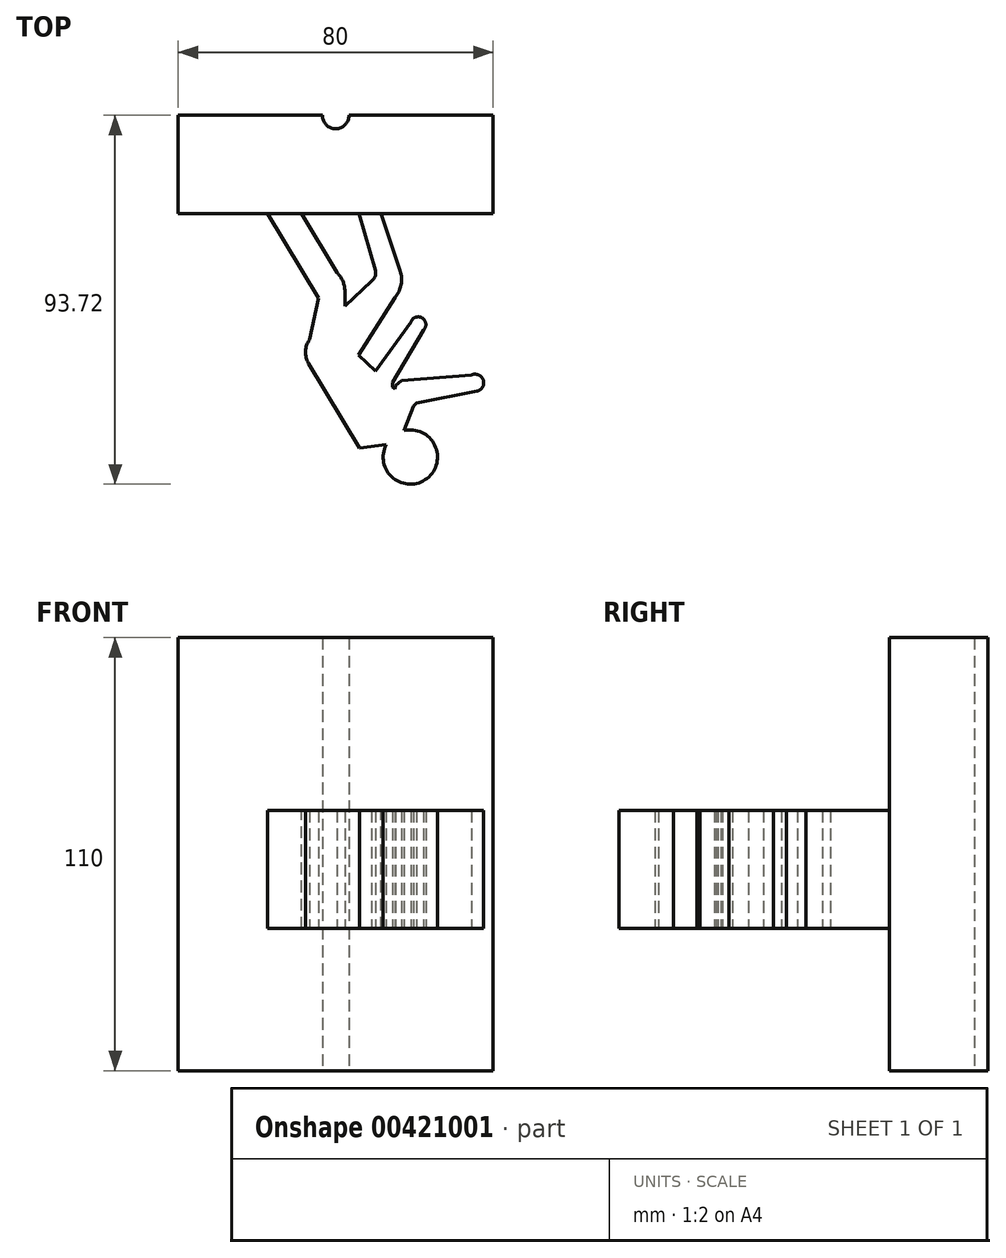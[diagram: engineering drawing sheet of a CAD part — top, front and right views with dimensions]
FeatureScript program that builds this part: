
annotation { "Feature Type Name" : "Feature", "Feature Type Description" : "" }
export const myFeature = defineFeature(function(context is Context, id is Id, definition is map)
    precondition{}
    {
        {
            var Q0;
            Q0=qCreatedBy(makeId("Front.planeOp"),FACE);
            var sketch = newSketch(context, id + "F0", { "sketchPlane" : qUnion([Q0])});
            skLineSegment(sketch, "E0.bottom", {"start": v(31.86, -51.09) * mm, "end": v(-48.14, -51.09) * mm});
            skLineSegment(sketch, "E0.top", {"start": v(31.86, 58.91) * mm, "end": v(-48.14, 58.91) * mm});
            skLineSegment(sketch, "E0.left", {"start": v(31.86, -51.09) * mm, "end": v(31.86, 58.91) * mm});
            skLineSegment(sketch, "E0.right", {"start": v(-48.14, -51.09) * mm, "end": v(-48.14, 58.91) * mm});
            skPoint(sketch, "E0.middle", {"position": v(-8.14, 3.91) * mm});
            skSolve(sketch);
        }
        {
            var Q0;
            Q0 = qSketchRegion(id + "F0", true);
            extrude(context, id + "F1", {"entities" : qUnion([Q0]), "depth" : 25 * mm});
        }
        {
            var Q0;
            Q0=makeQuery(id+"F1.opExtrude","SWEPT_FACE",FACE,{"disambiguationData":[OSD([sQuery(id+"F0.wireOp",EDGE,"E0.bottom")])]});
            var sketch = newSketch(context, id + "F2", { "sketchPlane" : qUnion([Q0])});
            skCircle(sketch, "E1", {"center": v(-8.14, 0) * mm, "radius": 3.4 * mm});
            skSolve(sketch);
        }
        {
            var Q0;
            {var subQ0=sQuery(id+"F2.wireOp",EDGE,"E1");var subQ1=makeQuery(id+"F1.opExtrude","CAP_EDGE",EDGE,{"disambiguationData":[OSD([sQuery(id+"F0.wireOp",EDGE,"E0.bottom")])],"isStart":true});var subQ2=makeQuery(id+"F2.imprint","INTERSECT",VERTEX,{"disambiguationData":[OD(0.0)],"derivedFrom":[subQ1,subQ0]});Q0=makeQuery(id+"F2.imprint","IMPRINT",FACE,{"disambiguationData":[TD([[makeQuery(id+"F2.imprint","IMPRINT",EDGE,{"disambiguationData":[TD([[subQ2,1.0]])],"derivedFrom":subQ0}),1.0]])]});}
            var Q1;
            {var subQ0=sQuery(id+"F2.wireOp",EDGE,"E1");var subQ1=makeQuery(id+"F1.opExtrude","CAP_EDGE",EDGE,{"disambiguationData":[OSD([sQuery(id+"F0.wireOp",EDGE,"E0.bottom")])],"isStart":true});var subQ2=makeQuery(id+"F2.imprint","INTERSECT",VERTEX,{"disambiguationData":[OD(0.0)],"derivedFrom":[subQ1,subQ0]});Q1=makeQuery(id+"F2.imprint","IMPRINT",FACE,{"disambiguationData":[TD([[makeQuery(id+"F2.imprint","IMPRINT",EDGE,{"disambiguationData":[TD([[subQ2,-1.0]])],"derivedFrom":subQ0}),1.0]])]});}
            extrude(context, id + "F3", {"entities" : qUnion([Q0, Q1]), "operationType" : NewBodyOperationType.REMOVE, "oppositeDirection" : true, "depth" : 122.9 * mm});
        }
        {
            var Q0;
            Q0=qCreatedBy(makeId("Top.planeOp"),FACE);
            var sketch = newSketch(context, id + "F4", { "sketchPlane" : qUnion([Q0])});
            skLineSegment(sketch, "E2", {"start": v(-12.54, -46.37) * mm, "end": v(-25.62, -24.68) * mm});
            skLineSegment(sketch, "E3", {"start": v(-17.04, -24.68) * mm, "end": v(-7.8, -40) * mm});
            skLineSegment(sketch, "E4", {"start": v(-14.79, -56.99) * mm, "end": v(-12.54, -46.37) * mm});
            skLineSegment(sketch, "E5", {"start": v(-5.8, -48.45) * mm, "end": v(0.9, -42.08) * mm});
            skLineSegment(sketch, "E6", {"start": v(1.95, -39.46) * mm, "end": v(-2.34, -24.68) * mm});
            skLineSegment(sketch, "E7", {"start": v(-2.34, -24.68) * mm, "end": v(3.24, -24.68) * mm});
            skLineSegment(sketch, "E8", {"start": v(3.24, -24.68) * mm, "end": v(8.23, -39.46) * mm});
            skLineSegment(sketch, "E9", {"start": v(-2.34, -60.9) * mm, "end": v(1.95, -64.94) * mm});
            skLineSegment(sketch, "E10", {"start": v(1.95, -64.94) * mm, "end": v(10.97, -52.5) * mm});
            skLineSegment(sketch, "E11", {"start": v(14.2, -54.53) * mm, "end": v(6.32, -67.9) * mm});
            skLineSegment(sketch, "E12", {"start": v(6.32, -67.9) * mm, "end": v(6.32, -69.05) * mm});
            skLineSegment(sketch, "E13", {"start": v(6.32, -69.05) * mm, "end": v(6.94, -69.5) * mm});
            skLineSegment(sketch, "E14", {"start": v(6.94, -69.5) * mm, "end": v(7.12, -68.63) * mm});
            skLineSegment(sketch, "E15", {"start": v(11.63, -73.92) * mm, "end": v(12.37, -73.12) * mm});
            skLineSegment(sketch, "E16", {"start": v(12.37, -73.12) * mm, "end": v(27.71, -70.1) * mm});
            skLineSegment(sketch, "E17", {"start": v(7.12, -68.63) * mm, "end": v(8.52, -67.43) * mm});
            skLineSegment(sketch, "E18", {"start": v(8.52, -67.43) * mm, "end": v(26.33, -66) * mm});
            skLineSegment(sketch, "E19", {"start": v(-2.03, -84.55) * mm, "end": v(-15.02, -63.01) * mm});
            skLineSegment(sketch, "E20", {"start": v(-15.02, -63.01) * mm, "end": v(-2.03, -84.55) * mm});
            skLineSegment(sketch, "E21", {"start": v(-2.03, -84.55) * mm, "end": v(4.7, -83.67) * mm});
            skLineSegment(sketch, "E22", {"start": v(9.21, -80.12) * mm, "end": v(11.63, -73.92) * mm});
            skLineSegment(sketch, "E23", {"start": v(-5.8, -48.45) * mm, "end": v(-5.8, -44.73) * mm});
            skArc(sketch, "E24", {"start": v(-5.8, -44.73) * mm, "mid": v(-6.32, -42.16) * mm, "end": v(-7.8, -40) * mm});
            skArc(sketch, "E25", {"start": v(0.9, -42.08) * mm, "mid": v(1.88, -40.95) * mm, "end": v(1.95, -39.46) * mm});
            skArc(sketch, "E26", {"start": v(14.2, -54.53) * mm, "mid": v(13.87, -51.5) * mm, "end": v(10.97, -52.5) * mm});
            skArc(sketch, "E27", {"start": v(27.71, -70.1) * mm, "mid": v(29.36, -67.25) * mm, "end": v(26.33, -66) * mm});
            skArc(sketch, "E28", {"start": v(4.7, -83.67) * mm, "mid": v(15.09, -92.24) * mm, "end": v(9.21, -80.12) * mm});
            skLineSegment(sketch, "E29", {"start": v(-2.34, -60.9) * mm, "end": v(6.97, -46.28) * mm});
            skArc(sketch, "E30", {"start": v(6.97, -46.28) * mm, "mid": v(8.48, -43.03) * mm, "end": v(8.23, -39.46) * mm});
            skPoint(sketch, "E31.end.orphan", {"position": v(-0.92, -70.82) * mm});
            skPoint(sketch, "E32.orphan", {"position": v(-1.13, -72.86) * mm});
            skPoint(sketch, "E33.end.orphan", {"position": v(-0.71, -68.78) * mm});
            skLineSegment(sketch, "E34", {"start": v(-25.62, -24.68) * mm, "end": v(-17.04, -24.68) * mm});
            skArc(sketch, "E35", {"start": v(-14.79, -56.99) * mm, "mid": v(-15.8, -59.97) * mm, "end": v(-15.02, -63.01) * mm});
            skSolve(sketch);
        }
        {
            var Q0;
            Q0=makeQuery(id+"F4.imprint","IMPRINT",FACE,{"disambiguationData":[TD([[makeQuery(id+"F4.imprint","IMPRINT",EDGE,{"derivedFrom":sQuery(id+"F4.wireOp",EDGE,"E2")}),-1.0]])]});
            extrude(context, id + "F5", {"entities" : qUnion([Q0]), "operationType" : NewBodyOperationType.ADD, "endBound" : BoundingType.SYMMETRIC, "depth" : 30 * mm});
        }
    });
